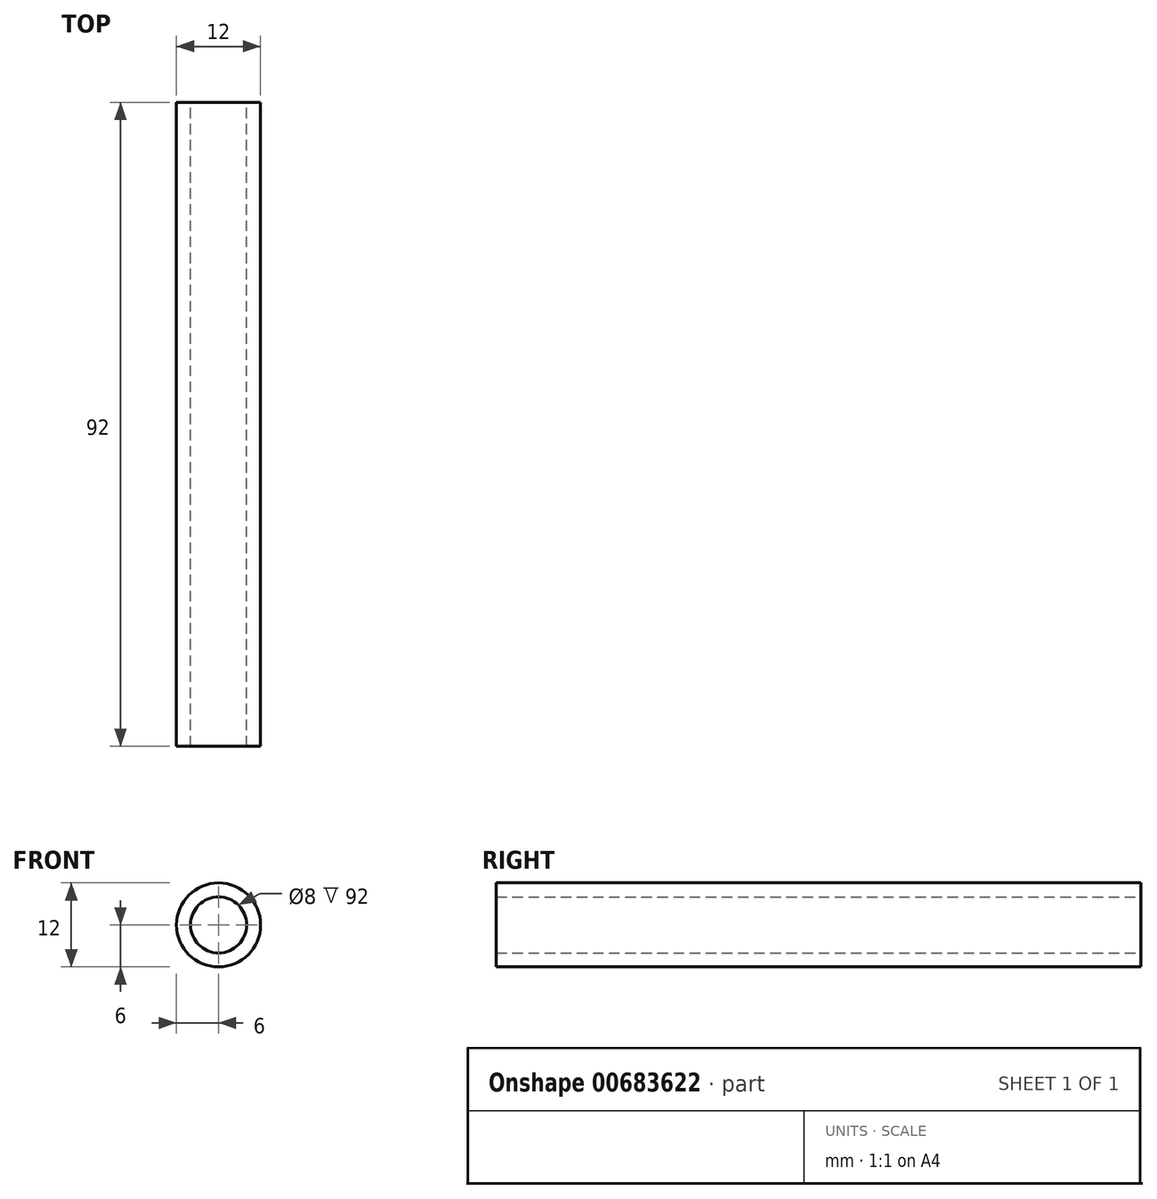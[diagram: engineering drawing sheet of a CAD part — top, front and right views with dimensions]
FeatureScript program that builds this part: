
annotation { "Feature Type Name" : "Feature", "Feature Type Description" : "" }
export const myFeature = defineFeature(function(context is Context, id is Id, definition is map)
    precondition{}
    {
        {
            var Q0;
            Q0=qCreatedBy(makeId("Front.planeOp"),FACE);
            var sketch = newSketch(context, id + "F0", { "sketchPlane" : qUnion([Q0])});
            skCircle(sketch, "E0", {"center": v(0, 0) * mm, "radius": 6 * mm});
            skCircle(sketch, "E1", {"center": v(0, 0) * mm, "radius": 4 * mm});
            skSolve(sketch);
        }
        {
            var Q0;
            Q0=qSketchRegion(id+"F0",true);
            extrude(context, id + "F1", {"entities" : qUnion([Q0]), "depth" : 92 * mm, "offsetDistance" : 25 * mm});
        }
    });
